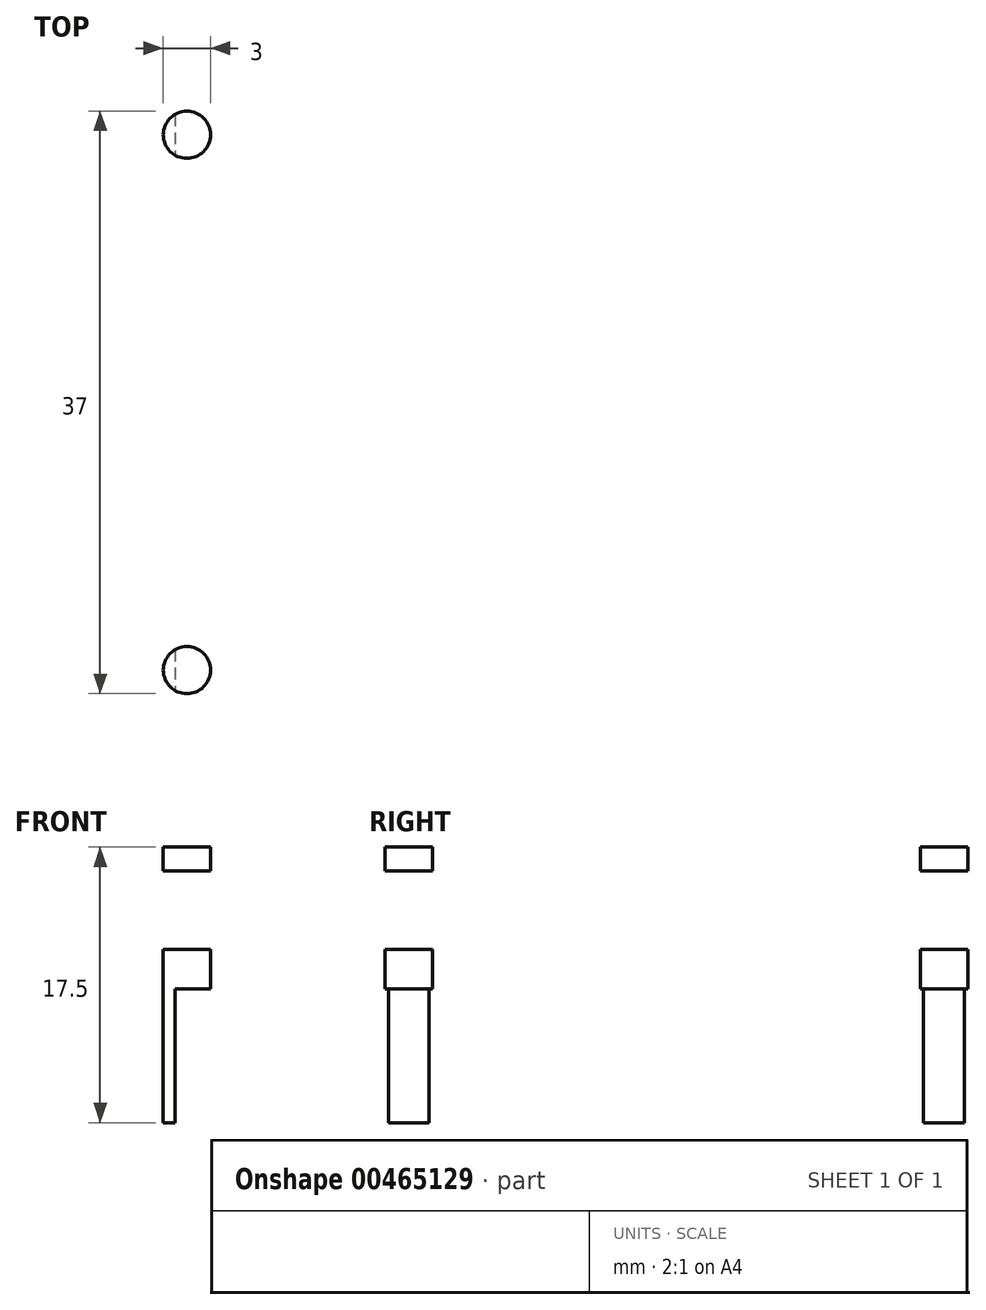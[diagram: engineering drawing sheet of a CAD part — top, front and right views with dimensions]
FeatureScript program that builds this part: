
annotation { "Feature Type Name" : "Feature", "Feature Type Description" : "" }
export const myFeature = defineFeature(function(context is Context, id is Id, definition is map)
    precondition{}
    {
        {
            var Q0;
            Q0=qCreatedBy(makeId("Top.planeOp"),FACE);
            var sketch = newSketch(context, id + "F0", { "sketchPlane" : qUnion([Q0])});
            skLineSegment(sketch, "E0.bottom", {"start": v(37.5, -25) * mm, "end": v(-37.5, -25) * mm});
            skLineSegment(sketch, "E0.top", {"start": v(37.5, 25) * mm, "end": v(-37.5, 25) * mm});
            skLineSegment(sketch, "E0.left", {"start": v(37.5, -25) * mm, "end": v(37.5, 25) * mm});
            skLineSegment(sketch, "E0.right", {"start": v(-37.5, -25) * mm, "end": v(-37.5, 25) * mm});
            skLineSegment(sketch, "E1.bottom", {"start": v(37.5, 0) * mm, "end": v(27.5, 0) * mm});
            skLineSegment(sketch, "E1.top", {"start": v(37.5, 15) * mm, "end": v(27.5, 15) * mm});
            skLineSegment(sketch, "E1.left", {"start": v(37.5, 0) * mm, "end": v(37.5, 15) * mm});
            skLineSegment(sketch, "E1.right", {"start": v(27.5, 0) * mm, "end": v(27.5, 15) * mm});
            skPoint(sketch, "E1.middle", {"position": v(32.5, 7.5) * mm});
            skCircle(sketch, "E2", {"center": v(35, 22.5) * mm, "radius": 2 * mm});
            skLineSegment(sketch, "E3.MirrorCS", {"start": v(37.5, 0) * mm, "end": v(37.5, -15) * mm});
            skLineSegment(sketch, "E4.MirrorCS", {"start": v(37.5, -15) * mm, "end": v(27.5, -15) * mm});
            skLineSegment(sketch, "E5.MirrorCS", {"start": v(27.5, 0) * mm, "end": v(27.5, -15) * mm});
            skCircle(sketch, "E6.MirrorC", {"center": v(35, -22.5) * mm, "radius": 2 * mm});
            skPoint(sketch, "E7.MirrorP", {"position": v(32.5, -7.5) * mm});
            skLineSegment(sketch, "E8.MirrorCS", {"start": v(-37.5, 0) * mm, "end": v(-27.5, 0) * mm});
            skLineSegment(sketch, "E9.MirrorCS", {"start": v(-37.5, -15) * mm, "end": v(-27.5, -15) * mm});
            skLineSegment(sketch, "E10.MirrorCS", {"start": v(-27.5, 0) * mm, "end": v(-27.5, -15) * mm});
            skPoint(sketch, "E11.MirrorP", {"position": v(-32.5, -7.5) * mm});
            skCircle(sketch, "E12.MirrorC", {"center": v(-35, -22.5) * mm, "radius": 2 * mm});
            skPoint(sketch, "E13.MirrorP", {"position": v(-32.5, 7.5) * mm});
            skLineSegment(sketch, "E14.MirrorCS", {"start": v(-37.5, 0) * mm, "end": v(-37.5, -15) * mm});
            skLineSegment(sketch, "E15.MirrorCS", {"start": v(-37.5, 0) * mm, "end": v(-37.5, 15) * mm});
            skLineSegment(sketch, "E16.MirrorCS", {"start": v(-37.5, 15) * mm, "end": v(-27.5, 15) * mm});
            skCircle(sketch, "E17.MirrorC", {"center": v(-35, 22.5) * mm, "radius": 2 * mm});
            skLineSegment(sketch, "E18.MirrorCS", {"start": v(-27.5, 0) * mm, "end": v(-27.5, 15) * mm});
            skCircle(sketch, "E19", {"center": v(-24.5, 20) * mm, "radius": 5 * mm});
            skCircle(sketch, "E20", {"center": v(2.5, 21.5) * mm, "radius": 3.5 * mm});
            skLineSegment(sketch, "E21.bottom", {"start": v(27.4, -25) * mm, "end": v(10.4, -25) * mm});
            skLineSegment(sketch, "E21.top", {"start": v(27.4, -15) * mm, "end": v(10.4, -15) * mm});
            skLineSegment(sketch, "E21.left", {"start": v(27.4, -25) * mm, "end": v(27.4, -15) * mm});
            skLineSegment(sketch, "E21.right", {"start": v(10.4, -25) * mm, "end": v(10.4, -15) * mm});
            skPoint(sketch, "E21.middle", {"position": v(18.9, -20) * mm});
            skLineSegment(sketch, "E22.bottom", {"start": v(7.4, -24.5) * mm, "end": v(4.4, -24.5) * mm});
            skLineSegment(sketch, "E22.top", {"start": v(7.4, -15.5) * mm, "end": v(4.4, -15.5) * mm});
            skLineSegment(sketch, "E22.left", {"start": v(7.4, -24.5) * mm, "end": v(7.4, -15.5) * mm});
            skLineSegment(sketch, "E22.right", {"start": v(4.4, -24.5) * mm, "end": v(4.4, -15.5) * mm});
            skPoint(sketch, "E22.middle", {"position": v(5.9, -20) * mm});
            skLineSegment(sketch, "E23.1.0.0", {"start": v(1.4, -24.5) * mm, "end": v(1.4, -15.5) * mm});
            skLineSegment(sketch, "E23.1.0.1", {"start": v(-1.6, -24.5) * mm, "end": v(-1.6, -15.5) * mm});
            skLineSegment(sketch, "E23.1.0.2", {"start": v(1.4, -24.5) * mm, "end": v(-1.6, -24.5) * mm});
            skLineSegment(sketch, "E23.1.0.3", {"start": v(1.4, -15.5) * mm, "end": v(-1.6, -15.5) * mm});
            skPoint(sketch, "E23.1.0.4", {"position": v(-0.1, -20) * mm});
            skLineSegment(sketch, "E23.2.0.0", {"start": v(-4.6, -24.5) * mm, "end": v(-4.6, -15.5) * mm});
            skLineSegment(sketch, "E23.2.0.1", {"start": v(-7.6, -24.5) * mm, "end": v(-7.6, -15.5) * mm});
            skLineSegment(sketch, "E23.2.0.2", {"start": v(-4.6, -24.5) * mm, "end": v(-7.6, -24.5) * mm});
            skLineSegment(sketch, "E23.2.0.3", {"start": v(-4.6, -15.5) * mm, "end": v(-7.6, -15.5) * mm});
            skPoint(sketch, "E23.2.0.4", {"position": v(-6.1, -20) * mm});
            skLineSegment(sketch, "E23.direction1", {"start": v(4.4, -24.5) * mm, "end": v(-1.6, -24.5) * mm, "construction": true});
            skSolve(sketch);
        }
        {
            var Q0;
            {var subQ14=sQuery(id+"F0.wireOp",EDGE,"E1.top");Q0=makeQuery(id+"F0.imprint","IMPRINT",FACE,{"disambiguationData":[TD([[makeQuery(id+"F0.imprint","IMPRINT",EDGE,{"derivedFrom":subQ14}),-1.0]])]});}
            var Q1;
            {var subQ0=sQuery(id+"F0.wireOp",EDGE,"E4.MirrorCS");Q1=makeQuery(id+"F0.imprint","IMPRINT",FACE,{"disambiguationData":[TD([[makeQuery(id+"F0.imprint","IMPRINT",EDGE,{"derivedFrom":subQ0}),1.0]])]});}
            var Q2;
            Q2=makeQuery(id+"F0.imprint","IMPRINT",FACE,{"disambiguationData":[TD([[makeQuery(id+"F0.imprint","IMPRINT",EDGE,{"derivedFrom":sQuery(id+"F0.wireOp",EDGE,"E1.bottom")}),1.0]])]});
            var Q3;
            Q3=makeQuery(id+"F0.imprint","IMPRINT",FACE,{"disambiguationData":[TD([[makeQuery(id+"F0.imprint","IMPRINT",EDGE,{"derivedFrom":sQuery(id+"F0.wireOp",EDGE,"E1.top")}),1.0]])]});
            var Q4;
            {var subQ0=sQuery(id+"F0.wireOp",EDGE,"E9.MirrorCS");Q4=makeQuery(id+"F0.imprint","IMPRINT",FACE,{"disambiguationData":[TD([[makeQuery(id+"F0.imprint","IMPRINT",EDGE,{"derivedFrom":subQ0}),1.0]])]});}
            var Q5;
            {var subQ0=sQuery(id+"F0.wireOp",EDGE,"E16.MirrorCS");Q5=makeQuery(id+"F0.imprint","IMPRINT",FACE,{"disambiguationData":[TD([[makeQuery(id+"F0.imprint","IMPRINT",EDGE,{"derivedFrom":subQ0}),-1.0]])]});}
            var Q6;
            Q6=makeQuery(id+"F0.imprint","IMPRINT",FACE,{"disambiguationData":[TD([[makeQuery(id+"F0.imprint","IMPRINT",EDGE,{"derivedFrom":sQuery(id+"F0.wireOp",EDGE,"E19")}),1.0]])]});
            var Q7;
            Q7=makeQuery(id+"F0.imprint","IMPRINT",FACE,{"disambiguationData":[TD([[makeQuery(id+"F0.imprint","IMPRINT",EDGE,{"derivedFrom":sQuery(id+"F0.wireOp",EDGE,"E20")}),1.0]])]});
            var Q8;
            Q8=makeQuery(id+"F0.imprint","IMPRINT",FACE,{"disambiguationData":[TD([[makeQuery(id+"F0.imprint","IMPRINT",EDGE,{"derivedFrom":sQuery(id+"F0.wireOp",EDGE,"E22.bottom")}),-1.0]])]});
            var Q9;
            Q9=makeQuery(id+"F0.imprint","IMPRINT",FACE,{"disambiguationData":[TD([[makeQuery(id+"F0.imprint","IMPRINT",EDGE,{"derivedFrom":sQuery(id+"F0.wireOp",EDGE,"E23.1.0.0")}),1.0]])]});
            var Q10;
            Q10=makeQuery(id+"F0.imprint","IMPRINT",FACE,{"disambiguationData":[TD([[makeQuery(id+"F0.imprint","IMPRINT",EDGE,{"derivedFrom":sQuery(id+"F0.wireOp",EDGE,"E23.2.0.0")}),1.0]])]});
            var Q11;
            Q11=makeQuery(id+"F0.imprint","IMPRINT",FACE,{"disambiguationData":[TD([[makeQuery(id+"F0.imprint","IMPRINT",EDGE,{"derivedFrom":sQuery(id+"F0.wireOp",EDGE,"E21.bottom")}),-1.0]])]});
            extrude(context, id + "F1", {"entities" : qUnion([Q0, Q1, Q2, Q3, Q4, Q5, Q6, Q7, Q8, Q9, Q10, Q11]), "oppositeDirection" : true, "depth" : 1.5 * mm});
        }
        {
            var Q0;
            {var subQ0=sQuery(id+"F0.wireOp",EDGE,"E16.MirrorCS");Q0=makeQuery(id+"F0.imprint","IMPRINT",FACE,{"disambiguationData":[TD([[makeQuery(id+"F0.imprint","IMPRINT",EDGE,{"derivedFrom":subQ0}),-1.0]])]});}
            var Q1;
            {var subQ0=sQuery(id+"F0.wireOp",EDGE,"E9.MirrorCS");Q1=makeQuery(id+"F0.imprint","IMPRINT",FACE,{"disambiguationData":[TD([[makeQuery(id+"F0.imprint","IMPRINT",EDGE,{"derivedFrom":subQ0}),1.0]])]});}
            var Q2;
            Q2=makeQuery(id+"F0.imprint","IMPRINT",FACE,{"disambiguationData":[TD([[makeQuery(id+"F0.imprint","IMPRINT",EDGE,{"derivedFrom":sQuery(id+"F0.wireOp",EDGE,"E1.bottom")}),1.0]])]});
            var Q3;
            Q3=makeQuery(id+"F0.imprint","IMPRINT",FACE,{"disambiguationData":[TD([[makeQuery(id+"F0.imprint","IMPRINT",EDGE,{"derivedFrom":sQuery(id+"F0.wireOp",EDGE,"E1.top")}),1.0]])]});
            extrude(context, id + "F2", {"entities" : qUnion([Q0, Q1, Q2, Q3]), "operationType" : NewBodyOperationType.ADD, "depth" : 7 * mm});
        }
        {
            var Q0;
            Q0=makeQuery(id+"F0.imprint","IMPRINT",FACE,{"disambiguationData":[TD([[makeQuery(id+"F0.imprint","IMPRINT",EDGE,{"derivedFrom":sQuery(id+"F0.wireOp",EDGE,"E23.2.0.0")}),1.0]])]});
            var Q1;
            Q1=makeQuery(id+"F0.imprint","IMPRINT",FACE,{"disambiguationData":[TD([[makeQuery(id+"F0.imprint","IMPRINT",EDGE,{"derivedFrom":sQuery(id+"F0.wireOp",EDGE,"E23.1.0.0")}),1.0]])]});
            var Q2;
            Q2=makeQuery(id+"F0.imprint","IMPRINT",FACE,{"disambiguationData":[TD([[makeQuery(id+"F0.imprint","IMPRINT",EDGE,{"derivedFrom":sQuery(id+"F0.wireOp",EDGE,"E22.bottom")}),-1.0]])]});
            var Q3;
            Q3=makeQuery(id+"F0.imprint","IMPRINT",FACE,{"disambiguationData":[TD([[makeQuery(id+"F0.imprint","IMPRINT",EDGE,{"derivedFrom":sQuery(id+"F0.wireOp",EDGE,"E21.bottom")}),-1.0]])]});
            extrude(context, id + "F3", {"entities" : qUnion([Q0, Q1, Q2, Q3]), "operationType" : NewBodyOperationType.ADD, "depth" : 5 * mm});
        }
        {
            var Q0;
            Q0=makeQuery(id+"F2.opExtrude","SWEPT_FACE",FACE,{"disambiguationData":[OSD([sQuery(id+"F0.wireOp",EDGE,"E9.MirrorCS")])]});
            var sketch = newSketch(context, id + "F4", { "sketchPlane" : qUnion([Q0])});
            skLineSegment(sketch, "E24", {"start": v(-35.5, 15) * mm, "end": v(-29.5, 15) * mm});
            skLineSegment(sketch, "E25", {"start": v(-29.5, 15) * mm, "end": v(-27.5, 7) * mm});
            skLineSegment(sketch, "E26", {"start": v(-27.5, 7) * mm, "end": v(-37.5, 7) * mm});
            skLineSegment(sketch, "E27", {"start": v(-37.5, 7) * mm, "end": v(-35.5, 15) * mm});
            skPoint(sketch, "E28", {"position": v(-32.5, 15) * mm});
            skPoint(sketch, "E29", {"position": v(-32.5, 7) * mm});
            skLineSegment(sketch, "E30.MirrorCS", {"start": v(35.5, 15) * mm, "end": v(29.5, 15) * mm});
            skLineSegment(sketch, "E31.MirrorCS", {"start": v(37.5, 7) * mm, "end": v(35.5, 15) * mm});
            skPoint(sketch, "E32.MirrorP", {"position": v(32.5, 15) * mm});
            skLineSegment(sketch, "E33.MirrorCS", {"start": v(27.5, 7) * mm, "end": v(37.5, 7) * mm});
            skLineSegment(sketch, "E34.MirrorCS", {"start": v(29.5, 15) * mm, "end": v(27.5, 7) * mm});
            skPoint(sketch, "E35.MirrorP", {"position": v(32.5, 7) * mm});
            skSolve(sketch);
        }
        {
            var Q0;
            Q0=makeQuery(id+"F4.imprint","IMPRINT",FACE,{"disambiguationData":[TD([[makeQuery(id+"F4.imprint","IMPRINT",EDGE,{"derivedFrom":sQuery(id+"F4.wireOp",EDGE,"E24")}),-1.0]])]});
            var Q1;
            Q1=makeQuery(id+"F4.imprint","IMPRINT",FACE,{"disambiguationData":[TD([[makeQuery(id+"F4.imprint","IMPRINT",EDGE,{"derivedFrom":sQuery(id+"F4.wireOp",EDGE,"E30.MirrorCS")}),1.0]])]});
            var Q2;
            Q2=makeQuery(id+"F2.opExtrude","SWEPT_FACE",FACE,{"disambiguationData":[OSD([sQuery(id+"F0.wireOp",EDGE,"E16.MirrorCS")])]});
            extrude(context, id + "F5", {"entities" : qUnion([Q0, Q1]), "operationType" : NewBodyOperationType.ADD, "endBound" : BoundingType.UP_TO_SURFACE, "oppositeDirection" : true, "endBoundEntityFace" : qUnion([Q2]), "depth" : 25 * mm});
        }
        {
            var Q0;
            Q0=makeQuery(id+"F0.imprint","IMPRINT",FACE,{"disambiguationData":[TD([[makeQuery(id+"F0.imprint","IMPRINT",EDGE,{"derivedFrom":sQuery(id+"F0.wireOp",EDGE,"E19")}),1.0]])]});
            extrude(context, id + "F6", {"entities" : qUnion([Q0]), "operationType" : NewBodyOperationType.ADD, "depth" : 18 * mm});
        }
        {
            var Q0;
            Q0=makeQuery(id+"F0.imprint","IMPRINT",FACE,{"disambiguationData":[TD([[makeQuery(id+"F0.imprint","IMPRINT",EDGE,{"derivedFrom":sQuery(id+"F0.wireOp",EDGE,"E20")}),1.0]])]});
            extrude(context, id + "F7", {"entities" : qUnion([Q0]), "operationType" : NewBodyOperationType.ADD, "depth" : 12 * mm});
        }
        {
            var Q0;
            Q0=makeQuery(id+"F1.opExtrude","CAP_FACE",FACE,{"disambiguationData":[OSD([sQuery(id+"F0.wireOp",EDGE,"E0.bottom"),sQuery(id+"F0.wireOp",EDGE,"E0.top"),sQuery(id+"F0.wireOp",EDGE,"E0.left"),sQuery(id+"F0.wireOp",EDGE,"E1.left"),sQuery(id+"F0.wireOp",EDGE,"E2"),sQuery(id+"F0.wireOp",EDGE,"E3.MirrorCS"),sQuery(id+"F0.wireOp",EDGE,"E6.MirrorC"),sQuery(id+"F0.wireOp",EDGE,"E12.MirrorC"),sQuery(id+"F0.wireOp",EDGE,"E0.right"),sQuery(id+"F0.wireOp",EDGE,"E17.MirrorC"),sQuery(id+"F0.wireOp",EDGE,"E21.bottom")])],"isStart":false});
            var sketch = newSketch(context, id + "F8", { "sketchPlane" : qUnion([Q0])});
            skLineSegment(sketch, "E36.bottom", {"start": v(-7, 18) * mm, "end": v(-22, 18) * mm});
            skLineSegment(sketch, "E36.top", {"start": v(-7, -18) * mm, "end": v(-22, -18) * mm});
            skLineSegment(sketch, "E36.left", {"start": v(-7, 18) * mm, "end": v(-7, -18) * mm});
            skLineSegment(sketch, "E36.right", {"start": v(-22, 18) * mm, "end": v(-22, -18) * mm});
            skPoint(sketch, "E36.middle", {"position": v(-14.5, 0) * mm});
            skCircle(sketch, "E37", {"center": v(-14.5, 17) * mm, "radius": 1.5 * mm});
            skCircle(sketch, "E38.MirrorC", {"center": v(-14.5, -17) * mm, "radius": 1.5 * mm});
            skSolve(sketch);
        }
        {
            var Q0;
            Q0=makeQuery(id+"F8.imprint","IMPRINT",FACE,{"disambiguationData":[TD([[makeQuery(id+"F8.imprint","IMPRINT",EDGE,{"derivedFrom":sQuery(id+"F8.wireOp",EDGE,"E36.bottom")}),1.0]])]});
            extrude(context, id + "F9", {"entities" : qUnion([Q0]), "depth" : 5 * mm});
        }
        {
            var Q0;
            Q0=makeQuery(id+"F9.opExtrude","CAP_FACE",FACE,{"disambiguationData":[OSD([sQuery(id+"F8.wireOp",EDGE,"E36.bottom"),sQuery(id+"F8.wireOp",EDGE,"E36.top"),sQuery(id+"F8.wireOp",EDGE,"E36.left"),sQuery(id+"F8.wireOp",EDGE,"E36.right")])],"isStart":false});
            var sketch = newSketch(context, id + "F10", { "sketchPlane" : qUnion([Q0])});
            skLineSegment(sketch, "E39.bottom", {"start": v(-32.5, 25) * mm, "end": v(7.5, 25) * mm});
            skLineSegment(sketch, "E39.top", {"start": v(-32.5, -25) * mm, "end": v(7.5, -25) * mm});
            skLineSegment(sketch, "E39.left", {"start": v(-32.5, 25) * mm, "end": v(-32.5, -25) * mm});
            skLineSegment(sketch, "E39.right", {"start": v(7.5, 25) * mm, "end": v(7.5, -25) * mm});
            skPoint(sketch, "E39.middle", {"position": v(-12.5, 0) * mm});
            skPoint(sketch, "E39.middle.positionSnap0", {"position": v(-22, 0) * mm});
            skPoint(sketch, "E39.centerSnap0", {"position": v(-22, 0) * mm});
            skSolve(sketch);
        }
        {
            var Q0;
            Q0=makeQuery(id+"F10.imprint","IMPRINT",FACE,{"disambiguationData":[TD([[makeQuery(id+"F10.imprint","IMPRINT",EDGE,{"derivedFrom":sQuery(id+"F10.wireOp",EDGE,"E39.bottom")}),-1.0]])]});
            var Q1;
            Q1=makeQuery(id+"F10.imprint","IMPRINT",FACE,{"disambiguationData":[TD([[makeQuery(id+"F10.imprint","IMPRINT",EDGE,{"derivedFrom":makeQuery(id+"F9.opExtrude","CAP_EDGE",EDGE,{"disambiguationData":[OSD([sQuery(id+"F8.wireOp",EDGE,"E36.bottom")])],"isStart":false})}),1.0]])]});
            extrude(context, id + "F11", {"entities" : qUnion([Q0, Q1]), "depth" : 2.5 * mm});
        }
        {
            var Q0;
            Q0=makeQuery(id+"F11.opExtrude","CAP_FACE",FACE,{"disambiguationData":[OSD([sQuery(id+"F10.wireOp",EDGE,"E39.bottom"),sQuery(id+"F10.wireOp",EDGE,"E39.top"),sQuery(id+"F10.wireOp",EDGE,"E39.left"),sQuery(id+"F10.wireOp",EDGE,"E39.right")])],"isStart":false});
            var sketch = newSketch(context, id + "F12", { "sketchPlane" : qUnion([Q0])});
            skLineSegment(sketch, "E40.bottom", {"start": v(7.5, -25) * mm, "end": v(6.5, -25) * mm});
            skLineSegment(sketch, "E40.top", {"start": v(7.5, 25) * mm, "end": v(6.5, 25) * mm});
            skLineSegment(sketch, "E40.left", {"start": v(7.5, -25) * mm, "end": v(7.5, 25) * mm});
            skLineSegment(sketch, "E40.right", {"start": v(6.5, -25) * mm, "end": v(6.5, 25) * mm});
            skLineSegment(sketch, "E41.1.0.0", {"start": v(4.25, -25) * mm, "end": v(4.25, 25) * mm});
            skLineSegment(sketch, "E41.1.0.1", {"start": v(3.25, -25) * mm, "end": v(3.25, 25) * mm});
            skLineSegment(sketch, "E41.1.0.2", {"start": v(4.25, 25) * mm, "end": v(3.25, 25) * mm});
            skLineSegment(sketch, "E41.1.0.3", {"start": v(4.25, -25) * mm, "end": v(3.25, -25) * mm});
            skLineSegment(sketch, "E41.2.0.0", {"start": v(1, -25) * mm, "end": v(1, 25) * mm});
            skLineSegment(sketch, "E41.2.0.1", {"start": v(0, -25) * mm, "end": v(0, 25) * mm});
            skLineSegment(sketch, "E41.2.0.2", {"start": v(1, 25) * mm, "end": v(0, 25) * mm});
            skLineSegment(sketch, "E41.2.0.3", {"start": v(1, -25) * mm, "end": v(0, -25) * mm});
            skLineSegment(sketch, "E41.3.0.0", {"start": v(-2.25, -25) * mm, "end": v(-2.25, 25) * mm});
            skLineSegment(sketch, "E41.3.0.1", {"start": v(-3.25, -25) * mm, "end": v(-3.25, 25) * mm});
            skLineSegment(sketch, "E41.3.0.2", {"start": v(-2.25, 25) * mm, "end": v(-3.25, 25) * mm});
            skLineSegment(sketch, "E41.3.0.3", {"start": v(-2.25, -25) * mm, "end": v(-3.25, -25) * mm});
            skLineSegment(sketch, "E41.4.0.0", {"start": v(-5.5, -25) * mm, "end": v(-5.5, 25) * mm});
            skLineSegment(sketch, "E41.4.0.1", {"start": v(-6.5, -25) * mm, "end": v(-6.5, 25) * mm});
            skLineSegment(sketch, "E41.4.0.2", {"start": v(-5.5, 25) * mm, "end": v(-6.5, 25) * mm});
            skLineSegment(sketch, "E41.4.0.3", {"start": v(-5.5, -25) * mm, "end": v(-6.5, -25) * mm});
            skLineSegment(sketch, "E41.5.0.0", {"start": v(-8.75, -25) * mm, "end": v(-8.75, 25) * mm});
            skLineSegment(sketch, "E41.5.0.1", {"start": v(-9.75, -25) * mm, "end": v(-9.75, 25) * mm});
            skLineSegment(sketch, "E41.5.0.2", {"start": v(-8.75, 25) * mm, "end": v(-9.75, 25) * mm});
            skLineSegment(sketch, "E41.5.0.3", {"start": v(-8.75, -25) * mm, "end": v(-9.75, -25) * mm});
            skLineSegment(sketch, "E41.6.0.0", {"start": v(-12, -25) * mm, "end": v(-12, 25) * mm});
            skLineSegment(sketch, "E41.6.0.1", {"start": v(-13, -25) * mm, "end": v(-13, 25) * mm});
            skLineSegment(sketch, "E41.6.0.2", {"start": v(-12, 25) * mm, "end": v(-13, 25) * mm});
            skLineSegment(sketch, "E41.6.0.3", {"start": v(-12, -25) * mm, "end": v(-13, -25) * mm});
            skLineSegment(sketch, "E41.7.0.0", {"start": v(-15.25, -25) * mm, "end": v(-15.25, 25) * mm});
            skLineSegment(sketch, "E41.7.0.1", {"start": v(-16.25, -25) * mm, "end": v(-16.25, 25) * mm});
            skLineSegment(sketch, "E41.7.0.2", {"start": v(-15.25, 25) * mm, "end": v(-16.25, 25) * mm});
            skLineSegment(sketch, "E41.7.0.3", {"start": v(-15.25, -25) * mm, "end": v(-16.25, -25) * mm});
            skLineSegment(sketch, "E41.8.0.0", {"start": v(-18.5, -25) * mm, "end": v(-18.5, 25) * mm});
            skLineSegment(sketch, "E41.8.0.1", {"start": v(-19.5, -25) * mm, "end": v(-19.5, 25) * mm});
            skLineSegment(sketch, "E41.8.0.2", {"start": v(-18.5, 25) * mm, "end": v(-19.5, 25) * mm});
            skLineSegment(sketch, "E41.8.0.3", {"start": v(-18.5, -25) * mm, "end": v(-19.5, -25) * mm});
            skLineSegment(sketch, "E41.9.0.0", {"start": v(-21.75, -25) * mm, "end": v(-21.75, 25) * mm});
            skLineSegment(sketch, "E41.9.0.1", {"start": v(-22.75, -25) * mm, "end": v(-22.75, 25) * mm});
            skLineSegment(sketch, "E41.9.0.2", {"start": v(-21.75, 25) * mm, "end": v(-22.75, 25) * mm});
            skLineSegment(sketch, "E41.9.0.3", {"start": v(-21.75, -25) * mm, "end": v(-22.75, -25) * mm});
            skLineSegment(sketch, "E41.10.0.0", {"start": v(-25, -25) * mm, "end": v(-25, 25) * mm});
            skLineSegment(sketch, "E41.10.0.1", {"start": v(-26, -25) * mm, "end": v(-26, 25) * mm});
            skLineSegment(sketch, "E41.10.0.2", {"start": v(-25, 25) * mm, "end": v(-26, 25) * mm});
            skLineSegment(sketch, "E41.10.0.3", {"start": v(-25, -25) * mm, "end": v(-26, -25) * mm});
            skLineSegment(sketch, "E41.11.0.0", {"start": v(-28.25, -25) * mm, "end": v(-28.25, 25) * mm});
            skLineSegment(sketch, "E41.11.0.1", {"start": v(-29.25, -25) * mm, "end": v(-29.25, 25) * mm});
            skLineSegment(sketch, "E41.11.0.2", {"start": v(-28.25, 25) * mm, "end": v(-29.25, 25) * mm});
            skLineSegment(sketch, "E41.11.0.3", {"start": v(-28.25, -25) * mm, "end": v(-29.25, -25) * mm});
            skLineSegment(sketch, "E41.12.0.0", {"start": v(-31.5, -25) * mm, "end": v(-31.5, 25) * mm});
            skLineSegment(sketch, "E41.12.0.1", {"start": v(-32.5, -25) * mm, "end": v(-32.5, 25) * mm});
            skLineSegment(sketch, "E41.12.0.2", {"start": v(-31.5, 25) * mm, "end": v(-32.5, 25) * mm});
            skLineSegment(sketch, "E41.12.0.3", {"start": v(-31.5, -25) * mm, "end": v(-32.5, -25) * mm});
            skLineSegment(sketch, "E41.direction1", {"start": v(6.5, -25) * mm, "end": v(3.25, -25) * mm, "construction": true});
            skSolve(sketch);
        }
        {
            var Q0;
            Q0=makeQuery(id+"F12.imprint","IMPRINT",FACE,{"disambiguationData":[TD([[makeQuery(id+"F12.imprint","IMPRINT",EDGE,{"derivedFrom":sQuery(id+"F12.wireOp",EDGE,"E40.bottom")}),1.0]])]});
            var Q1;
            Q1=makeQuery(id+"F12.imprint","IMPRINT",FACE,{"disambiguationData":[TD([[makeQuery(id+"F12.imprint","IMPRINT",EDGE,{"derivedFrom":sQuery(id+"F12.wireOp",EDGE,"E41.1.0.0")}),1.0]])]});
            var Q2;
            Q2=makeQuery(id+"F12.imprint","IMPRINT",FACE,{"disambiguationData":[TD([[makeQuery(id+"F12.imprint","IMPRINT",EDGE,{"derivedFrom":sQuery(id+"F12.wireOp",EDGE,"E41.2.0.0")}),1.0]])]});
            var Q3;
            Q3=makeQuery(id+"F12.imprint","IMPRINT",FACE,{"disambiguationData":[TD([[makeQuery(id+"F12.imprint","IMPRINT",EDGE,{"derivedFrom":sQuery(id+"F12.wireOp",EDGE,"E41.3.0.0")}),1.0]])]});
            var Q4;
            Q4=makeQuery(id+"F12.imprint","IMPRINT",FACE,{"disambiguationData":[TD([[makeQuery(id+"F12.imprint","IMPRINT",EDGE,{"derivedFrom":sQuery(id+"F12.wireOp",EDGE,"E41.4.0.0")}),1.0]])]});
            var Q5;
            Q5=makeQuery(id+"F12.imprint","IMPRINT",FACE,{"disambiguationData":[TD([[makeQuery(id+"F12.imprint","IMPRINT",EDGE,{"derivedFrom":sQuery(id+"F12.wireOp",EDGE,"E41.5.0.0")}),1.0]])]});
            var Q6;
            Q6=makeQuery(id+"F12.imprint","IMPRINT",FACE,{"disambiguationData":[TD([[makeQuery(id+"F12.imprint","IMPRINT",EDGE,{"derivedFrom":sQuery(id+"F12.wireOp",EDGE,"E41.6.0.0")}),1.0]])]});
            var Q7;
            Q7=makeQuery(id+"F12.imprint","IMPRINT",FACE,{"disambiguationData":[TD([[makeQuery(id+"F12.imprint","IMPRINT",EDGE,{"derivedFrom":sQuery(id+"F12.wireOp",EDGE,"E41.7.0.0")}),1.0]])]});
            var Q8;
            Q8=makeQuery(id+"F12.imprint","IMPRINT",FACE,{"disambiguationData":[TD([[makeQuery(id+"F12.imprint","IMPRINT",EDGE,{"derivedFrom":sQuery(id+"F12.wireOp",EDGE,"E41.8.0.0")}),1.0]])]});
            var Q9;
            Q9=makeQuery(id+"F12.imprint","IMPRINT",FACE,{"disambiguationData":[TD([[makeQuery(id+"F12.imprint","IMPRINT",EDGE,{"derivedFrom":sQuery(id+"F12.wireOp",EDGE,"E41.9.0.0")}),1.0]])]});
            var Q10;
            Q10=makeQuery(id+"F12.imprint","IMPRINT",FACE,{"disambiguationData":[TD([[makeQuery(id+"F12.imprint","IMPRINT",EDGE,{"derivedFrom":sQuery(id+"F12.wireOp",EDGE,"E41.10.0.0")}),1.0]])]});
            var Q11;
            Q11=makeQuery(id+"F12.imprint","IMPRINT",FACE,{"disambiguationData":[TD([[makeQuery(id+"F12.imprint","IMPRINT",EDGE,{"derivedFrom":sQuery(id+"F12.wireOp",EDGE,"E41.11.0.0")}),1.0]])]});
            var Q12;
            Q12=makeQuery(id+"F12.imprint","IMPRINT",FACE,{"disambiguationData":[TD([[makeQuery(id+"F12.imprint","IMPRINT",EDGE,{"derivedFrom":sQuery(id+"F12.wireOp",EDGE,"E41.12.0.0")}),1.0]])]});
            extrude(context, id + "F13", {"entities" : qUnion([Q0, Q1, Q2, Q3, Q4, Q5, Q6, Q7, Q8, Q9, Q10, Q11, Q12]), "operationType" : NewBodyOperationType.ADD, "depth" : (11 - 2.5) * mm});
        }
        {
            var Q0;
            {var subQ0=sQuery(id+"F8.wireOp",EDGE,"E37");var subQ1=sQuery(id+"F8.wireOp",EDGE,"E36.bottom");var subQ2=makeQuery(id+"F8.imprint","INTERSECT",VERTEX,{"disambiguationData":[OD(0.0)],"derivedFrom":[subQ1,subQ0]});Q0=makeQuery(id+"F8.imprint","IMPRINT",FACE,{"disambiguationData":[TD([[makeQuery(id+"F8.imprint","IMPRINT",EDGE,{"disambiguationData":[TD([[subQ2,-1.0]])],"derivedFrom":subQ1}),1.0]])]});}
            var Q1;
            {var subQ0=sQuery(id+"F8.wireOp",EDGE,"E37");var subQ1=sQuery(id+"F8.wireOp",EDGE,"E36.bottom");var subQ2=makeQuery(id+"F8.imprint","INTERSECT",VERTEX,{"disambiguationData":[OD(0.0)],"derivedFrom":[subQ1,subQ0]});Q1=makeQuery(id+"F8.imprint","IMPRINT",FACE,{"disambiguationData":[TD([[makeQuery(id+"F8.imprint","IMPRINT",EDGE,{"disambiguationData":[TD([[subQ2,-1.0]])],"derivedFrom":subQ1}),-1.0]])]});}
            var Q2;
            {var subQ0=sQuery(id+"F8.wireOp",EDGE,"E38.MirrorC");var subQ1=sQuery(id+"F8.wireOp",EDGE,"E36.top");var subQ2=makeQuery(id+"F8.imprint","INTERSECT",VERTEX,{"disambiguationData":[OD(0.0)],"derivedFrom":[subQ1,subQ0]});Q2=makeQuery(id+"F8.imprint","IMPRINT",FACE,{"disambiguationData":[TD([[makeQuery(id+"F8.imprint","IMPRINT",EDGE,{"disambiguationData":[TD([[subQ2,-1.0]])],"derivedFrom":subQ1}),-1.0]])]});}
            var Q3;
            {var subQ0=sQuery(id+"F8.wireOp",EDGE,"E38.MirrorC");var subQ1=sQuery(id+"F8.wireOp",EDGE,"E36.top");var subQ2=makeQuery(id+"F8.imprint","INTERSECT",VERTEX,{"disambiguationData":[OD(0.0)],"derivedFrom":[subQ1,subQ0]});Q3=makeQuery(id+"F8.imprint","IMPRINT",FACE,{"disambiguationData":[TD([[makeQuery(id+"F8.imprint","IMPRINT",EDGE,{"disambiguationData":[TD([[subQ2,-1.0]])],"derivedFrom":subQ1}),1.0]])]});}
            extrude(context, id + "F14", {"entities" : qUnion([Q0, Q1, Q2, Q3]), "operationType" : NewBodyOperationType.REMOVE, "endBound" : BoundingType.SYMMETRIC, "oppositeDirection" : true, "depth" : 100 * mm});
        }
    });
